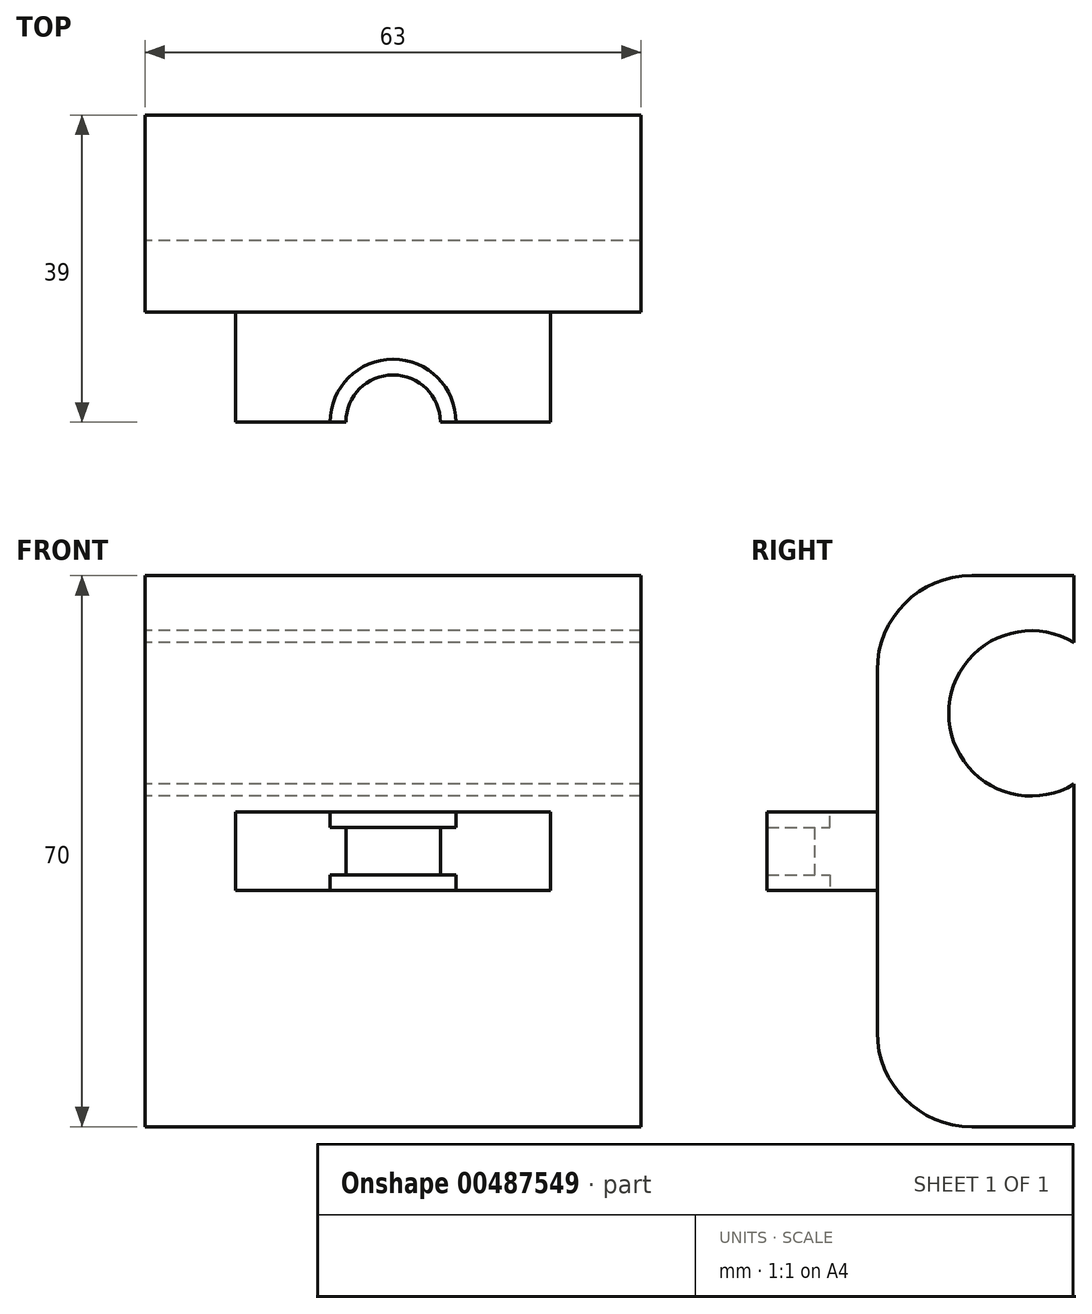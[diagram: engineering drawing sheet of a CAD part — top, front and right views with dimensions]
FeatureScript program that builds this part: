
annotation { "Feature Type Name" : "Feature", "Feature Type Description" : "" }
export const myFeature = defineFeature(function(context is Context, id is Id, definition is map)
    precondition{}
    {
        {
            var Q0;
            Q0=qCreatedBy(makeId("Front.planeOp"),FACE);
            var sketch = newSketch(context, id + "F0", { "sketchPlane" : qUnion([Q0])});
            skLineSegment(sketch, "E0.bottom", {"start": v(31.5, -35) * mm, "end": v(-31.5, -35) * mm});
            skLineSegment(sketch, "E0.top", {"start": v(31.5, 35) * mm, "end": v(-31.5, 35) * mm});
            skLineSegment(sketch, "E0.left", {"start": v(31.5, -35) * mm, "end": v(31.5, 35) * mm});
            skLineSegment(sketch, "E0.right", {"start": v(-31.5, -35) * mm, "end": v(-31.5, 35) * mm});
            skPoint(sketch, "E0.middle", {"position": v(0, 0) * mm});
            skSolve(sketch);
        }
        {
            var Q0;
            Q0 = qSketchRegion(id + "F0", true);
            extrude(context, id + "F1", {"entities" : qUnion([Q0]), "depth" : 25 * mm, "offsetDistance" : 25 * mm});
        }
        {
            var Q0;
            Q0=makeQuery(id+"F1.opExtrude","SWEPT_FACE",FACE,{"disambiguationData":[OSD([sQuery(id+"F0.wireOp",EDGE,"E0.right")])]});
            var sketch = newSketch(context, id + "F2", { "sketchPlane" : qUnion([Q0])});
            skLineSegment(sketch, "E1", {"start": v(0, 0) * mm, "end": v(25, 0) * mm, "construction": true});
            skLineSegment(sketch, "E2", {"start": v(5.42, 35) * mm, "end": v(5.42, -35) * mm, "construction": true});
            skCircle(sketch, "E3", {"center": v(5.42, 17.5) * mm, "radius": 10.5 * mm});
            skCircle(sketch, "E4.MirrorC", {"center": v(5.42, -17.5) * mm, "radius": 10.5 * mm});
            skSolve(sketch);
        }
        {
            var Q0;
            {var subQ0=sQuery(id+"F2.wireOp",EDGE,"E3");var subQ1=makeQuery(id+"F1.opExtrude","CAP_EDGE",EDGE,{"disambiguationData":[OSD([sQuery(id+"F0.wireOp",EDGE,"E0.right")])],"isStart":true});var subQ2=makeQuery(id+"F2.imprint","INTERSECT",VERTEX,{"disambiguationData":[OD(0.0)],"derivedFrom":[subQ1,subQ0]});Q0=makeQuery(id+"F2.imprint","IMPRINT",FACE,{"disambiguationData":[TD([[makeQuery(id+"F2.imprint","IMPRINT",EDGE,{"disambiguationData":[TD([[subQ2,1.0]])],"derivedFrom":subQ0}),1.0]])]});}
            var Q1;
            {var subQ0=sQuery(id+"F2.wireOp",EDGE,"E4.MirrorC");var subQ1=makeQuery(id+"F1.opExtrude","CAP_EDGE",EDGE,{"disambiguationData":[OSD([sQuery(id+"F0.wireOp",EDGE,"E0.right")])],"isStart":true});var subQ2=makeQuery(id+"F2.imprint","INTERSECT",VERTEX,{"disambiguationData":[OD(0.0)],"derivedFrom":[subQ1,subQ0]});Q1=makeQuery(id+"F2.imprint","IMPRINT",FACE,{"disambiguationData":[TD([[makeQuery(id+"F2.imprint","IMPRINT",EDGE,{"disambiguationData":[TD([[subQ2,1.0]])],"derivedFrom":subQ0}),-1.0]])]});}
            extrude(context, id + "F3", {"entities" : qUnion([Q0, Q1]), "operationType" : NewBodyOperationType.REMOVE, "endBound" : BoundingType.THROUGH_ALL, "oppositeDirection" : true, "depth" : 25 * mm, "offsetDistance" : 25 * mm});
        }
        {
            var Q0;
            Q0=makeQuery(id+"F1.opExtrude","CAP_FACE",FACE,{"disambiguationData":[OSD([sQuery(id+"F0.wireOp",EDGE,"E0.bottom"),sQuery(id+"F0.wireOp",EDGE,"E0.top"),sQuery(id+"F0.wireOp",EDGE,"E0.left"),sQuery(id+"F0.wireOp",EDGE,"E0.right")])],"isStart":false});
            var sketch = newSketch(context, id + "F4", { "sketchPlane" : qUnion([Q0])});
            skLineSegment(sketch, "E5.bottom", {"start": v(20, -5) * mm, "end": v(-20, -5) * mm});
            skLineSegment(sketch, "E5.top", {"start": v(20, 5) * mm, "end": v(-20, 5) * mm});
            skLineSegment(sketch, "E5.left", {"start": v(20, -5) * mm, "end": v(20, 5) * mm});
            skLineSegment(sketch, "E5.right", {"start": v(-20, -5) * mm, "end": v(-20, 5) * mm});
            skPoint(sketch, "E5.middle", {"position": v(0, 0) * mm});
            skSolve(sketch);
        }
        {
            var Q0;
            Q0=makeQuery(id+"F4.imprint","IMPRINT",FACE,{"disambiguationData":[TD([[makeQuery(id+"F4.imprint","IMPRINT",EDGE,{"derivedFrom":sQuery(id+"F4.wireOp",EDGE,"E5.bottom")}),-1.0]])]});
            extrude(context, id + "F5", {"entities" : qUnion([Q0]), "operationType" : NewBodyOperationType.ADD, "depth" : 14 * mm, "offsetDistance" : 25 * mm});
        }
        {
            var Q0;
            Q0=makeQuery(id+"F5.opExtrude","SWEPT_FACE",FACE,{"disambiguationData":[OSD([sQuery(id+"F4.wireOp",EDGE,"E5.bottom")])]});
            var sketch = newSketch(context, id + "F6", { "sketchPlane" : qUnion([Q0])});
            skCircle(sketch, "E6", {"center": v(0, 39) * mm, "radius": 8 * mm});
            skCircle(sketch, "E7", {"center": v(0, 39) * mm, "radius": 6 * mm});
            skSolve(sketch);
        }
        {
            var Q0;
            {var subQ0=sQuery(id+"F6.wireOp",EDGE,"E7");var subQ1=makeQuery(id+"F5.opExtrude","CAP_EDGE",EDGE,{"disambiguationData":[OSD([sQuery(id+"F4.wireOp",EDGE,"E5.bottom")])],"isStart":false});var subQ2=makeQuery(id+"F6.imprint","INTERSECT",VERTEX,{"disambiguationData":[OD(0.0)],"derivedFrom":[subQ1,subQ0]});Q0=makeQuery(id+"F6.imprint","IMPRINT",FACE,{"disambiguationData":[TD([[makeQuery(id+"F6.imprint","IMPRINT",EDGE,{"disambiguationData":[TD([[subQ2,1.0]])],"derivedFrom":subQ0}),1.0]])]});}
            extrude(context, id + "F7", {"entities" : qUnion([Q0]), "operationType" : NewBodyOperationType.REMOVE, "endBound" : BoundingType.THROUGH_ALL, "oppositeDirection" : true, "depth" : 25 * mm, "offsetDistance" : 25 * mm});
        }
        {
            var Q0;
            {var subQ0=sQuery(id+"F6.wireOp",EDGE,"E6");var subQ1=makeQuery(id+"F5.opExtrude","CAP_EDGE",EDGE,{"disambiguationData":[OSD([sQuery(id+"F4.wireOp",EDGE,"E5.bottom")])],"isStart":false});var subQ2=makeQuery(id+"F6.imprint","INTERSECT",VERTEX,{"disambiguationData":[OD(0.0)],"derivedFrom":[subQ1,subQ0]});Q0=makeQuery(id+"F6.imprint","IMPRINT",FACE,{"disambiguationData":[TD([[makeQuery(id+"F6.imprint","IMPRINT",EDGE,{"disambiguationData":[TD([[subQ2,1.0]])],"derivedFrom":subQ0}),1.0]])]});}
            extrude(context, id + "F8", {"entities" : qUnion([Q0]), "operationType" : NewBodyOperationType.REMOVE, "oppositeDirection" : true, "depth" : 2 * mm, "offsetDistance" : 25 * mm});
        }
        {
            var Q0;
            Q0=makeQuery(id+"F5.opExtrude","SWEPT_FACE",FACE,{"disambiguationData":[OSD([sQuery(id+"F4.wireOp",EDGE,"E5.top")])]});
            var sketch = newSketch(context, id + "F9", { "sketchPlane" : qUnion([Q0])});
            skCircle(sketch, "E8", {"center": v(0, -39) * mm, "radius": 8 * mm});
            skSolve(sketch);
        }
        {
            var Q0;
            Q0 = qSketchRegion(id + "F9", true);
            extrude(context, id + "F10", {"entities" : qUnion([Q0]), "operationType" : NewBodyOperationType.REMOVE, "oppositeDirection" : true, "depth" : 2 * mm, "offsetDistance" : 25 * mm});
        }
        {
            var Q0;
            Q0=makeQuery(id+"F1.opExtrude","CAP_EDGE",EDGE,{"disambiguationData":[OSD([sQuery(id+"F0.wireOp",EDGE,"E0.top")])],"isStart":false});
            var Q1;
            Q1=makeQuery(id+"F1.opExtrude","CAP_EDGE",EDGE,{"disambiguationData":[OSD([sQuery(id+"F0.wireOp",EDGE,"E0.bottom")])],"isStart":false});
            fillet(context, id + "F11", {"entities" : qUnion([Q0, Q1]), "radius" : 12 * mm, "tangentPropagation" : true, "allowEdgeOverflow" : false});
        }
    });
